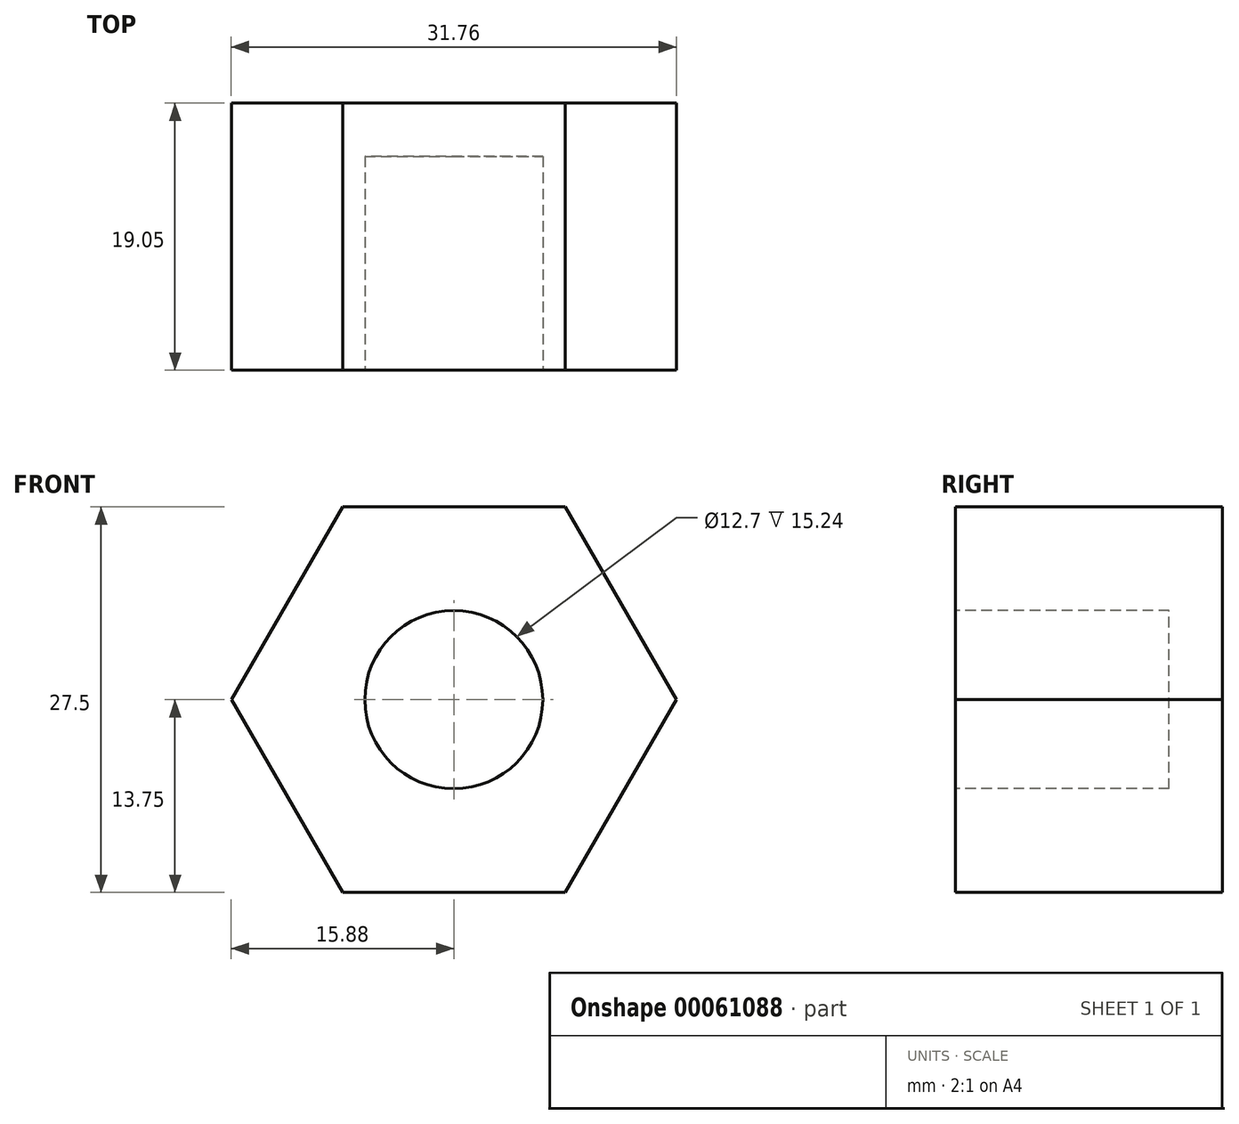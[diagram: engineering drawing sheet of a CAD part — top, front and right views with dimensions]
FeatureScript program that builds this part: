
annotation { "Feature Type Name" : "Feature", "Feature Type Description" : "" }
export const myFeature = defineFeature(function(context is Context, id is Id, definition is map)
    precondition{}
    {
        {
            var Q0;
            Q0=qCreatedBy(makeId("Front.planeOp"),FACE);
            var sketch = newSketch(context, id + "F0", { "sketchPlane" : qUnion([Q0])});
            skCircle(sketch, "E0.cCircle", {"center": v(0, 0) * mm, "radius": 13.75 * mm, "construction": true});
            skLineSegment(sketch, "E0.0", {"start": v(15.88, 0) * mm, "end": v(7.94, -13.75) * mm});
            skLineSegment(sketch, "E0.1", {"start": v(7.94, -13.75) * mm, "end": v(-7.94, -13.75) * mm});
            skLineSegment(sketch, "E0.2", {"start": v(-7.94, -13.75) * mm, "end": v(-15.88, 0) * mm});
            skLineSegment(sketch, "E0.3", {"start": v(-15.88, 0) * mm, "end": v(-7.94, 13.75) * mm});
            skLineSegment(sketch, "E0.4", {"start": v(-7.94, 13.75) * mm, "end": v(7.94, 13.75) * mm});
            skLineSegment(sketch, "E0.5", {"start": v(7.94, 13.75) * mm, "end": v(15.88, 0) * mm});
            skPoint(sketch, "E0.0.midPoint", {"position": v(11.9, -6.87) * mm});
            skSolve(sketch);
        }
        {
            var Q0;
            Q0 = qSketchRegion(id + "F0", true);
            extrude(context, id + "F1", {"entities" : qUnion([Q0]), "depth" : 19.05 * mm});
        }
        {
            var Q0;
            Q0=makeQuery(id+"F1.opExtrude","CAP_FACE",FACE,{"disambiguationData":[OSD([sQuery(id+"F0.wireOp",EDGE,"E0.0"),sQuery(id+"F0.wireOp",EDGE,"E0.1"),sQuery(id+"F0.wireOp",EDGE,"E0.2"),sQuery(id+"F0.wireOp",EDGE,"E0.3"),sQuery(id+"F0.wireOp",EDGE,"E0.4"),sQuery(id+"F0.wireOp",EDGE,"E0.5")])],"isStart":false});
            var sketch = newSketch(context, id + "F2", { "sketchPlane" : qUnion([Q0])});
            skCircle(sketch, "E1", {"center": v(0, 0) * mm, "radius": 6.35 * mm});
            skSolve(sketch);
        }
        {
            var Q0;
            Q0=makeQuery(id+"F2.imprint","IMPRINT",FACE,{"disambiguationData":[TD([[makeQuery(id+"F2.imprint","IMPRINT",EDGE,{"derivedFrom":sQuery(id+"F2.wireOp",EDGE,"E1")}),1.0]])]});
            extrude(context, id + "F3", {"entities" : qUnion([Q0]), "operationType" : NewBodyOperationType.REMOVE, "oppositeDirection" : true, "depth" : 15.24 * mm});
        }
    });
